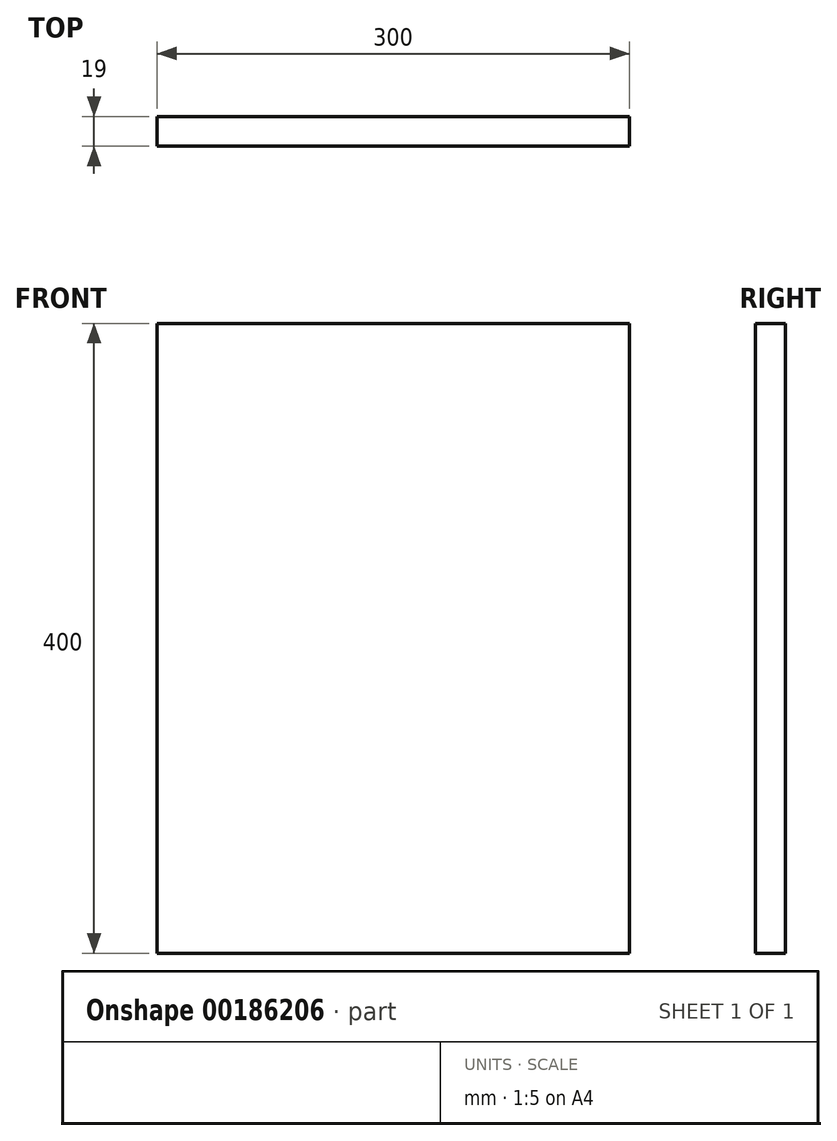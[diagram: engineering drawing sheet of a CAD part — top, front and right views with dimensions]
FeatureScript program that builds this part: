
annotation { "Feature Type Name" : "Feature", "Feature Type Description" : "" }
export const myFeature = defineFeature(function(context is Context, id is Id, definition is map)
    precondition{}
    {
        {
            var Q0;
            Q0=qCreatedBy(makeId("Front.planeOp"),FACE);
            var sketch = newSketch(context, id + "F0", { "sketchPlane" : qUnion([Q0])});
            skLineSegment(sketch, "E0.bottom", {"start": v(-146.4, 211.3) * mm, "end": v(153.6, 211.3) * mm});
            skLineSegment(sketch, "E0.top", {"start": v(-146.4, -188.7) * mm, "end": v(153.6, -188.7) * mm});
            skLineSegment(sketch, "E0.left", {"start": v(-146.4, 211.3) * mm, "end": v(-146.4, -188.7) * mm});
            skLineSegment(sketch, "E0.right", {"start": v(153.6, 211.3) * mm, "end": v(153.6, -188.7) * mm});
            skSolve(sketch);
        }
        {
            var Q0;
            Q0 = qSketchRegion(id + "F0", true);
            extrude(context, id + "F1", {"entities" : qUnion([Q0]), "depth" : 19 * mm});
        }
    });
